# Revit family: Trim_Kit_Shower-GROHE-Eurostyle-35062_Series
name_source: partatom
category: Plumbing Fixtures
revit_build: Autodesk Revit 2014 (Build: 20130308_1515(x64)
units: mm (PartAtom-declared; Revit-internal decimal feet)

## types (2) — shared parameters
ADA Compliant = No
Assembly Code = D2010710
CW Connection = Yes
CWFU = 3
Cold Water Connection Diameter = 1/2"
Cold Water Connection Radius = 1/4"
Default Elevation = 44"
Description = Eurostyle Pressure balance valve shower / bath combination
Flow Rate = 5.3 gpm (20 L/min)
HW Connection = Yes
HWFU = 3
Height = 40"
Hot Water Connection Diameter = 1"
Hot Water Connection Radius = 1/4"
Installation Type = Wall Mounted
Length = 3 1/8"
Manufacturer = Grohe
Price = Prices may vary. Please consult Manufacturer Representative for most up-to-date price list.
Product Page URL = https://www.grohe.us
Tempered Connection Diameter = 1/2"
Tempered Connection Radius = 1/4"
URL = https://www.grohe.us
Vent Connection = No
WFU = 4
Warranty Documentation Link = https://cdn.cloud.grohe.com
Waste Connection = No
Width = 6 11/16"

## per-type parameters (varying)
| type | Finish | Material |
| 35062003 | Metal-Grohe-003-Chrome | Metal-Grohe-003-Chrome |
| 35062EN3 | Metal-Grohe-EN3-Brushed Nickel | Metal-Grohe-EN3-Brushed Nickel |

note: column(s) folded — value = type name in every type: Model

## geometry (parser evidence)
native form markers: Sweep x1
no freeform markers — native parametric forms only
